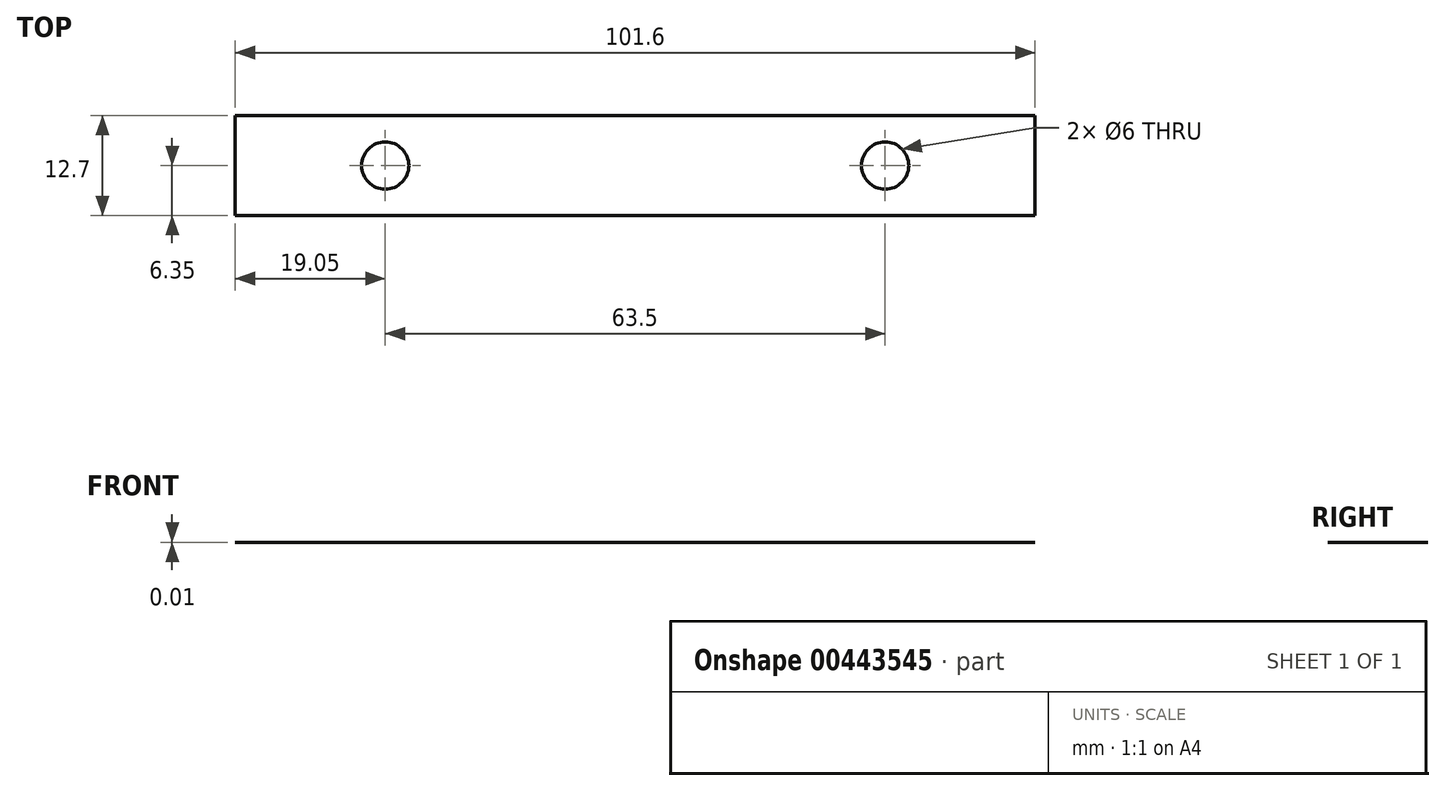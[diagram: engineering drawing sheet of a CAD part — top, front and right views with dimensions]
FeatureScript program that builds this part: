
annotation { "Feature Type Name" : "Feature", "Feature Type Description" : "" }
export const myFeature = defineFeature(function(context is Context, id is Id, definition is map)
    precondition{}
    {
        {
            var Q0;
            Q0=qCreatedBy(makeId("Top.planeOp"),FACE);
            var sketch = newSketch(context, id + "F0", { "sketchPlane" : qUnion([Q0])});
            skLineSegment(sketch, "E0.bottom", {"start": v(0, 0) * mm, "end": v(101.6, 0) * mm});
            skLineSegment(sketch, "E0.top", {"start": v(0, 12.7) * mm, "end": v(101.6, 12.7) * mm});
            skLineSegment(sketch, "E0.left", {"start": v(0, 0) * mm, "end": v(0, 12.7) * mm});
            skLineSegment(sketch, "E0.right", {"start": v(101.6, 0) * mm, "end": v(101.6, 12.7) * mm});
            skCircle(sketch, "E1", {"center": v(19.05, 6.35) * mm, "radius": 3 * mm});
            skCircle(sketch, "E2", {"center": v(82.55, 6.35) * mm, "radius": 3 * mm});
            skPoint(sketch, "E3", {"position": v(101.6, 6.35) * mm});
            skSolve(sketch);
        }
        {
            var Q0;
            Q0=makeQuery(id+"F0.imprint","IMPRINT",FACE,{"disambiguationData":[TD([[makeQuery(id+"F0.imprint","IMPRINT",EDGE,{"derivedFrom":sQuery(id+"F0.wireOp",EDGE,"E0.bottom")}),1.0]])]});
            extrude(context, id + "F1", {"entities" : qUnion([Q0]), "depth" : 1 / 101.6 * mm});
        }
    });
